# Revit family: Sensor-Lutron-Daylight-EcoSystem-EC-DIR-WH
name_source: partatom
category: Lighting Devices
revit_build: Autodesk Revit 2017 (Build: 20160720_1515(x64)
units: mm (PartAtom-declared; Revit-internal decimal feet)

## family parameters
Cut with Voids When Loaded = No
Host = Face
Maintain Annotation Orientation = No
OmniClass Number = 23.85.80.11.27
OmniClass Title = Lighting Controls
Part Type = Normal
Room Calculation Point = No
Round Connector Dimension = Use Diameter
Shared = No

## types (1)
- EC-DIR-WH
    Assembly Code = D5030800
    Cost = 0 $
    Default Elevation = 0' - 0"
    Description = Daylight Sensor
    Instruction Sheet Link = http://www.lutron.com
    Manufacturer = Lutron Electronics Co., Inc
    Manufacturer Fax Number = 610-282-1243
    Material = Plastic-Lutron-White-Gloss
    Model = EC-DIR-WH
    Nominal Height = 0' - 0 11/16"
    Nominal Length = 0' - 1 3/16"
    Nominal Width = 0' - 1 3/16"
    Performance URL = http://www.lutron.com
    Product Documentation Link = http://www.lutron.com
    Product Name = Daylight Sensor
    Product Page URL = http://www.lutron.com
    Series = EcoSystem
    URL = http://www.lutron.com
    Version = 2017 - v1.0b
    Video Link = https://www.youtube.com
    Voltage Comments = 0-20VDC
    Warranty URL = http://www.lutron.com

## geometry (parser evidence)
native form markers: Sweep x6
no freeform markers — native parametric forms only
